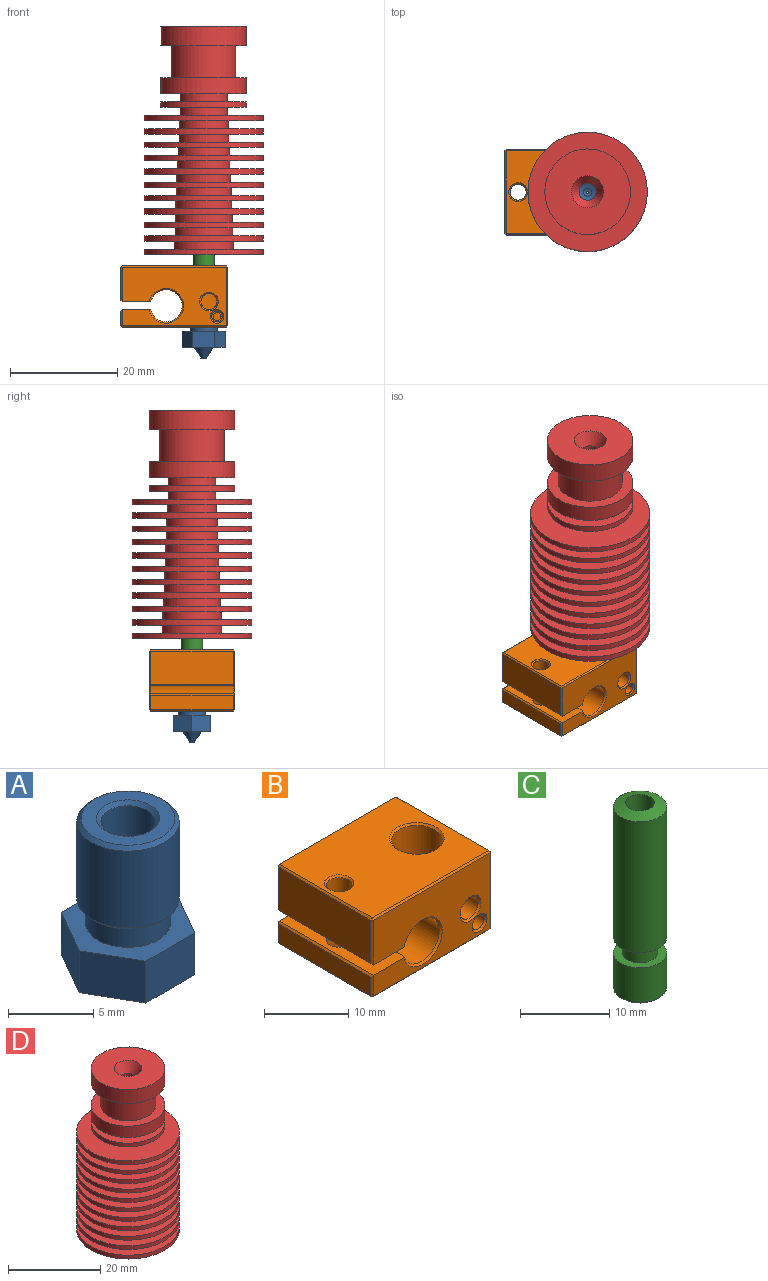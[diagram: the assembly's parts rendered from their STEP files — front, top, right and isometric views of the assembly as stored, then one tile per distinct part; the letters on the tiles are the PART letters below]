
ASSEMBLY  parts=4 mates=3
PART A: 22 faces, bbox 8.1x7x12.5 mm
  f0: cone r=2.75mm half-angle=45deg, axis (0,0,-1), area 6.4mm2, adj f1,f15
  f1: plane 5.5x5.5mm, normal (0,0,1), area 13mm2, adj f0,f2
  f2: cone r=1.6mm half-angle=45deg, axis (0,0,1), area 3.8mm2, adj f1,f3
  f3: cylinder r=1.6mm len=9.85mm, axis (0,0,1), area 99mm2, adj f2,f4
  f4: cone r=0.75mm half-angle=73.3deg, axis (0,0,1), area 6.6mm2, adj f3,f5
  f5: cylinder r=0.75mm len=1.5mm, axis (0,0,1), area 5.6mm2, adj f4,f6
  f6: cone r=0.2mm half-angle=73.3deg, axis (0,0,1), area 1.7mm2, adj f5,f7
  f7: cylinder r=0.2mm len=0.8mm, axis (0,0,1), area 1mm2, adj f6,f8
  f8: plane 1x1mm, normal (0,0,-1), area 0.7mm2, adj f7,f9
  f9: cone r=1.9mm half-angle=35deg, axis (0,0,1), area 18.4mm2, adj f8,f10
  f10: plane 8.08x7mm, normal (0,0,-1), area 31.1mm2, adj f9,f16,f17,f18,f19,f20,f21
  f11: plane 8.08x7mm, normal (0,0,1), area 22.8mm2, adj f12,f16,f17,f18,f19,f20,f21
  f12: cylinder r=2.5mm len=5mm, axis (0,0,1), area 23.6mm2, adj f11,f13
  f13: plane 5.5x5.5mm, normal (0,0,-1), area 4.1mm2, adj f12,f14
  f14: cone r=3mm half-angle=45deg, axis (0,0,1), area 6.4mm2, adj f13,f15
  f15: cylinder r=3mm len=6mm, axis (0,0,1), area 103.7mm2, adj f0,f14
  f16: plane 4.04x3mm, normal (0,-1,0), area 12.1mm2, adj f10,f11,f17,f19
  f17: plane 3.5x3mm, normal (0.87,-0.5,0), area 12.1mm2, adj f10,f11,f16,f18
  f18: plane 3.5x3mm, normal (0.87,0.5,0), area 12.1mm2, adj f10,f11,f17,f20
  f19: plane 3.5x3mm, normal (-0.87,-0.5,0), area 12.1mm2, adj f10,f11,f16,f21
  f20: plane 4.04x3mm, normal (0,1,0), area 12.1mm2, adj f10,f11,f18,f21
  f21: plane 3.5x3mm, normal (-0.87,0.5,0), area 12.1mm2, adj f10,f11,f19,f20
PART B: 55 faces, bbox 20x16x11.5 mm
  f0: plane 15.5x6.25mm, normal (-1,0,0), area 96.9mm2, adj f24,f27,f30,f31
  f1: plane 19.5x11mm, normal (0,-1,0), area 159.2mm2, adj f10,f11,f19,f20,f21,f27,f32,f39
  f2: cylinder r=1.5mm len=6.5mm, axis (0,0,1), area 61.3mm2, adj f10,f23
  f3: cylinder r=1.5mm len=3mm, axis (0,0,1), area 28.3mm2, adj f11,f54
  f4: plane 19.5x11mm, normal (0,1,0), area 171.2mm2, adj f25,f30,f34,f38,f41,f42,f45,f46
  f5: plane 15.5x2.75mm, normal (-1,0,0), area 42.6mm2, adj f45,f48,f51,f52
  f6: plane 15.5x11mm, normal (1,0,0), area 170.5mm2, adj f33,f34,f39,f40
  f7: cylinder r=3mm len=11mm, axis (0,0,1), area 207.3mm2, adj f22,f53
  f8: plane 19.5x15.5mm, normal (0,0,-1), area 259.4mm2, adj f40,f41,f47,f48,f53,f54
  f9: plane 19.5x15.5mm, normal (0,0,1), area 259.4mm2, adj f22,f23,f24,f25,f32,f33
  f10: plane 15.75x5.35mm, normal (0,0,-1), area 77.1mm2, adj f1,f2,f12,f19,f31,f38
  f11: plane 15.75x5.35mm, normal (0,0,1), area 77.1mm2, adj f1,f3,f12,f19,f46,f51
  f12: cylinder r=3mm len=15.5mm, axis (0,-1,0), area 268.7mm2, adj f10,f11,f19,f42
  f13: cylinder r=1.5mm len=3.25mm, axis (0,-1,0), area 30.6mm2, adj f14,f21
  f14: plane 3x3mm, normal (0,-1,0), area 7.1mm2, adj f13
  f15: cylinder r=1mm len=2mm, axis (0,-1,0), area 11mm2, adj f16,f20
  f16: plane 2x2mm, normal (0,-1,0), area 1.4mm2, adj f15,f18
  f17: plane 1.5x1.5mm, normal (0,-1,0), area 1.8mm2, adj f18
  f18: cylinder r=0.75mm len=2.5mm, axis (0,-1,0), area 11.8mm2, adj f16,f17
  f19: cone r=3mm half-angle=45deg, axis (0,-1,0), area 6.4mm2, adj f1,f10,f11,f12
  f20: cone r=1mm half-angle=45deg, axis (0,-1,0), area 2.5mm2, adj f1,f15
  f21: cone r=1.5mm half-angle=45deg, axis (0,-1,0), area 3.6mm2, adj f1,f13
  f22: cone r=3mm half-angle=45deg, axis (0,0,1), area 6.9mm2, adj f7,f9
  f23: cone r=1.5mm half-angle=45deg, axis (0,0,1), area 3.6mm2, adj f2,f9
  f24: plane 15.5x0.25mm, normal (-0.71,0,0.71), area 5.5mm2, adj f0,f9,f26,f28
  f25: plane 19.5x0.25mm, normal (0,0.71,0.71), area 6.9mm2, adj f4,f9,f26,f29
  f26: plane 0.25x0.25mm, normal (-0.58,0.58,0.58), area 0.1mm2, adj f24,f25,f30
  f27: plane 6.5x0.25mm, normal (-0.71,-0.71,0), area 2.3mm2, adj f0,f1,f28,f31
  f28: plane 0.25x0.25mm, normal (-0.58,-0.58,0.58), area 0.1mm2, adj f24,f27,f32
  f29: plane 0.25x0.25mm, normal (0.58,0.58,0.58), area 0.1mm2, adj f25,f33,f34
  f30: plane 6.25x0.25mm, normal (-0.71,0.71,0), area 2.2mm2, adj f0,f4,f26,f35
  f31: plane 15.75x0.25mm, normal (-0.71,0,-0.71), area 5.5mm2, adj f0,f10,f27,f35
  f32: plane 19.5x0.25mm, normal (0,-0.71,0.71), area 6.9mm2, adj f1,f9,f28,f36
  f33: plane 15.5x0.25mm, normal (0.71,0,0.71), area 5.5mm2, adj f6,f9,f29,f36
  f34: plane 11x0.25mm, normal (0.71,0.71,0), area 3.9mm2, adj f4,f6,f29,f37
  f35: plane 0.25x0.25mm, normal (-0.58,0.58,-0.58), area 0.1mm2, adj f30,f31,f38
  f36: plane 0.25x0.25mm, normal (0.58,-0.58,0.58), area 0.1mm2, adj f32,f33,f39
  f37: plane 0.25x0.25mm, normal (0.58,0.58,-0.58), area 0.1mm2, adj f34,f40,f41
  f38: plane 5.35x0.26mm, normal (0,0.71,-0.71), area 1.9mm2, adj f4,f10,f35,f42
  f39: plane 11x0.25mm, normal (0.71,-0.71,0), area 3.9mm2, adj f1,f6,f36,f43
  f40: plane 15.5x0.25mm, normal (0.71,0,-0.71), area 5.5mm2, adj f6,f8,f37,f43
  f41: plane 19.5x0.25mm, normal (0,0.71,-0.71), area 6.9mm2, adj f4,f8,f37,f44
  f42: cone r=3.25mm half-angle=45deg, axis (0,1,0), area 6.3mm2, adj f4,f12,f38,f46
  f43: plane 0.25x0.25mm, normal (0.58,-0.58,-0.58), area 0.1mm2, adj f39,f40,f47
  f44: plane 0.25x0.25mm, normal (-0.58,0.58,-0.58), area 0.1mm2, adj f41,f45,f48
  f45: plane 2.75x0.25mm, normal (-0.71,0.71,0), area 1mm2, adj f4,f5,f44,f49
  f46: plane 5.35x0.26mm, normal (0,0.71,0.71), area 1.9mm2, adj f4,f11,f42,f49
  f47: plane 19.5x0.25mm, normal (0,-0.71,-0.71), area 6.9mm2, adj f1,f8,f43,f50
  f48: plane 15.5x0.25mm, normal (-0.71,0,-0.71), area 5.5mm2, adj f5,f8,f44,f50
  f49: plane 0.25x0.25mm, normal (-0.58,0.58,0.58), area 0.1mm2, adj f45,f46,f51
  f50: plane 0.25x0.25mm, normal (-0.58,-0.58,-0.58), area 0.1mm2, adj f47,f48,f52
  f51: plane 15.75x0.25mm, normal (-0.71,0,0.71), area 5.5mm2, adj f5,f11,f49,f52
  f52: plane 3x0.25mm, normal (-0.71,-0.71,0), area 1mm2, adj f1,f5,f50,f51
  f53: cone r=3.25mm half-angle=45deg, axis (0,0,-1), area 6.9mm2, adj f7,f8
  f54: cone r=1.75mm half-angle=45deg, axis (0,0,-1), area 3.6mm2, adj f3,f8
PART C: 9 faces, bbox 6x6x25.6 mm
  f0: cone r=1.6mm half-angle=70deg, axis (0,0,-1), area 21.5mm2, adj f1,f8
  f1: cylinder r=1.6mm len=25.61mm, axis (0,0,1), area 257.5mm2, adj f0,f2
  f2: plane 5.5x5.5mm, normal (0,0,-1), area 15.7mm2, adj f1,f3
  f3: cone r=2.75mm half-angle=45deg, axis (0,0,1), area 6.4mm2, adj f2,f4
  f4: cylinder r=3mm len=6mm, axis (0,0,1), area 89.5mm2, adj f3,f5
  f5: plane 6x6mm, normal (0,0,1), area 15.7mm2, adj f4,f6
  f6: cylinder r=2mm len=4mm, axis (0,0,1), area 26.4mm2, adj f5,f7
  f7: plane 6x6mm, normal (0,0,-1), area 15.7mm2, adj f6,f8
  f8: cylinder r=3mm len=18mm, axis (0,0,1), area 339.3mm2, adj f0,f7
PART D: 59 faces, bbox 22.3x22.3x42.7 mm
  f0: cone r=1.6mm half-angle=70deg, axis (0,0,-1), area 21.5mm2, adj f1,f58
  f1: cylinder r=3mm len=18mm, axis (0,0,1), area 339.3mm2, adj f0,f2
  f2: plane 22.3x22.3mm, normal (0,0,-1), area 362.3mm2, adj f1,f3
  f3: cylinder r=11.15mm len=22.3mm, axis (0,0,1), area 70.1mm2, adj f2,f4
  f4: plane 22.3x22.3mm, normal (0,0,1), area 293.6mm2, adj f3,f5
  f5: cylinder r=5.56mm len=11.11mm, axis (0,0,1), area 52.4mm2, adj f4,f6
  f6: plane 22.3x22.3mm, normal (0,0,-1), area 293.6mm2, adj f5,f7
  f7: cylinder r=11.15mm len=22.3mm, axis (0,0,1), area 70.1mm2, adj f6,f8
  f8: plane 22.3x22.3mm, normal (0,0,1), area 297.4mm2, adj f7,f9
  f9: cylinder r=5.45mm len=10.89mm, axis (0,0,1), area 51.3mm2, adj f8,f10
  f10: plane 22.3x22.3mm, normal (0,0,-1), area 297.4mm2, adj f9,f11
  f11: cylinder r=11.15mm len=22.3mm, axis (0,0,1), area 70.1mm2, adj f10,f12
  f12: plane 22.3x22.3mm, normal (0,0,1), area 301.1mm2, adj f11,f13
  f13: cylinder r=5.34mm len=10.68mm, axis (0,0,1), area 50.3mm2, adj f12,f14
  f14: plane 22.3x22.3mm, normal (0,0,-1), area 301.1mm2, adj f13,f15
  f15: cylinder r=11.15mm len=22.3mm, axis (0,0,1), area 70.1mm2, adj f14,f16
  f16: plane 22.3x22.3mm, normal (0,0,1), area 304.7mm2, adj f15,f17
  f17: cylinder r=5.23mm len=10.46mm, axis (0,0,1), area 49.3mm2, adj f16,f18
  f18: plane 22.3x22.3mm, normal (0,0,-1), area 304.7mm2, adj f17,f19
  f19: cylinder r=11.15mm len=22.3mm, axis (0,0,1), area 70.1mm2, adj f18,f20
  f20: plane 22.3x22.3mm, normal (0,0,1), area 308.2mm2, adj f19,f21
  f21: cylinder r=5.12mm len=10.24mm, axis (0,0,1), area 48.3mm2, adj f20,f22
  f22: plane 22.3x22.3mm, normal (0,0,-1), area 308.2mm2, adj f21,f23
  f23: cylinder r=11.15mm len=22.3mm, axis (0,0,1), area 70.1mm2, adj f22,f24
  f24: plane 22.3x22.3mm, normal (0,0,1), area 311.7mm2, adj f23,f25
  f25: cylinder r=5.01mm len=10.02mm, axis (0,0,1), area 47.2mm2, adj f24,f26
  f26: plane 22.3x22.3mm, normal (0,0,-1), area 311.7mm2, adj f25,f27
  f27: cylinder r=11.15mm len=22.3mm, axis (0,0,1), area 70.1mm2, adj f26,f28
  f28: plane 22.3x22.3mm, normal (0,0,1), area 315.1mm2, adj f27,f29
  f29: cylinder r=4.9mm len=9.8mm, axis (0,0,1), area 46.2mm2, adj f28,f30
  f30: plane 22.3x22.3mm, normal (0,0,-1), area 315.1mm2, adj f29,f31
  f31: cylinder r=11.15mm len=22.3mm, axis (0,0,1), area 70.1mm2, adj f30,f32
  f32: plane 22.3x22.3mm, normal (0,0,1), area 318.4mm2, adj f31,f33
  f33: cylinder r=4.79mm len=9.58mm, axis (0,0,1), area 45.2mm2, adj f32,f34
  f34: plane 22.3x22.3mm, normal (0,0,-1), area 318.4mm2, adj f33,f35
  f35: cylinder r=11.15mm len=22.3mm, axis (0,0,1), area 70.1mm2, adj f34,f36
  f36: plane 22.3x22.3mm, normal (0,0,1), area 321.7mm2, adj f35,f37
  f37: cylinder r=4.68mm len=9.37mm, axis (0,0,1), area 44.1mm2, adj f36,f38
  f38: plane 22.3x22.3mm, normal (0,0,-1), area 321.7mm2, adj f37,f39
  f39: cylinder r=11.15mm len=22.3mm, axis (0,0,1), area 70.1mm2, adj f38,f40
  f40: plane 22.3x22.3mm, normal (0,0,1), area 324.8mm2, adj f39,f41
  f41: cylinder r=4.57mm len=9.15mm, axis (0,0,1), area 43.1mm2, adj f40,f42
  f42: plane 22.3x22.3mm, normal (0,0,-1), area 324.8mm2, adj f41,f43
  f43: cylinder r=11.15mm len=22.3mm, axis (0,0,1), area 70.1mm2, adj f42,f44
  f44: plane 22.3x22.3mm, normal (0,0,1), area 327.9mm2, adj f43,f45
  f45: cylinder r=4.46mm len=8.93mm, axis (0,0,1), area 42.1mm2, adj f44,f46
  f46: plane 16x16mm, normal (0,0,-1), area 138.4mm2, adj f45,f47
  f47: cylinder r=8mm len=16mm, axis (0,0,1), area 50.3mm2, adj f46,f48
  f48: plane 16x16mm, normal (0,0,1), area 138.4mm2, adj f47,f49
  f49: cylinder r=4.46mm len=8.93mm, axis (0,0,1), area 42.1mm2, adj f48,f50
  f50: plane 16x16mm, normal (0,0,-1), area 138.4mm2, adj f49,f51
  f51: cylinder r=8mm len=16mm, axis (0,0,1), area 150.8mm2, adj f50,f52
  f52: plane 16x16mm, normal (0,0,1), area 88mm2, adj f51,f53
  f53: cylinder r=6mm len=12mm, axis (0,0,1), area 226.2mm2, adj f52,f54
  f54: plane 16x16mm, normal (0,0,-1), area 88mm2, adj f53,f55
  f55: cylinder r=8mm len=16mm, axis (0,0,1), area 186mm2, adj f54,f56
  f56: plane 16x16mm, normal (0,0,1), area 172.8mm2, adj f55,f57
  f57: cone r=3mm half-angle=30deg, axis (0,0,1), area 40.5mm2, adj f56,f58
  f58: cylinder r=1.6mm len=21.77mm, axis (0,0,1), area 218.8mm2, adj f0,f57
PLACE A t=(37.53,12.96,11.1)mm
PLACE B t=(37.53,12.96,10.85)mm
PLACE C t=(37.53,12.96,10.85)mm
PLACE D t=(37.53,12.96,10.85)mm
MATE fastened C.f3 <-> B.f22  axis (0,0,1) through (37.53,12.96,8.75)mm
MATE fastened C.f3 <-> D.f1  axis (0,0,1) through (37.53,12.96,10.85)mm
MATE fastened C.f3 <-> A.f9  axis (0,0,1) through (37.53,12.96,4)mm
